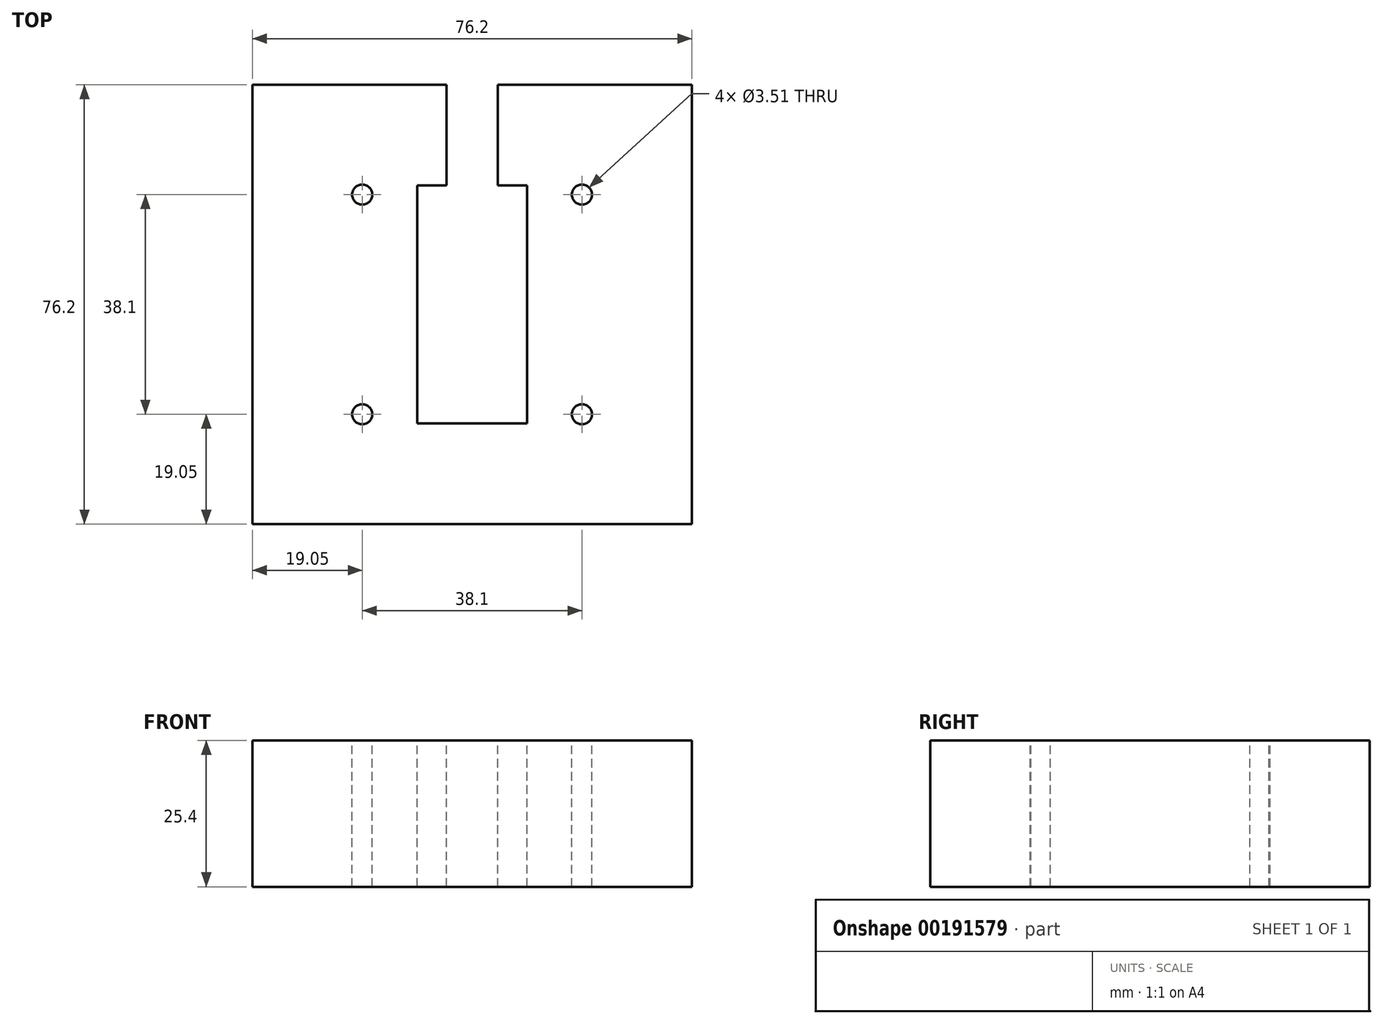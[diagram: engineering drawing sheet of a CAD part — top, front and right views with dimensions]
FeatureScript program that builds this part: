
annotation { "Feature Type Name" : "Feature", "Feature Type Description" : "" }
export const myFeature = defineFeature(function(context is Context, id is Id, definition is map)
    precondition{}
    {
        {
            var Q0;
            Q0=qCreatedBy(makeId("Top.planeOp"),FACE);
            var sketch = newSketch(context, id + "F0", { "sketchPlane" : qUnion([Q0])});
            skLineSegment(sketch, "E0.bottom", {"start": v(-38.1, 38.1) * mm, "end": v(38.1, 38.1) * mm});
            skLineSegment(sketch, "E0.top", {"start": v(-38.1, -38.1) * mm, "end": v(38.1, -38.1) * mm});
            skLineSegment(sketch, "E0.left", {"start": v(-38.1, 38.1) * mm, "end": v(-38.1, -38.1) * mm});
            skLineSegment(sketch, "E0.right", {"start": v(38.1, 38.1) * mm, "end": v(38.1, -38.1) * mm});
            skPoint(sketch, "E0.middle", {"position": v(0, 0) * mm});
            skSolve(sketch);
        }
        {
            var Q0;
            Q0 = qSketchRegion(id + "F0", true);
            extrude(context, id + "F1", {"entities" : qUnion([Q0]), "depth" : 25.4 * mm});
        }
        {
            var Q0;
            Q0=makeQuery(id+"F1.opExtrude","CAP_FACE",FACE,{"disambiguationData":[OSD([sQuery(id+"F0.wireOp",EDGE,"E0.bottom"),sQuery(id+"F0.wireOp",EDGE,"E0.top"),sQuery(id+"F0.wireOp",EDGE,"E0.left"),sQuery(id+"F0.wireOp",EDGE,"E0.right")])],"isStart":false});
            var sketch = newSketch(context, id + "F2", { "sketchPlane" : qUnion([Q0])});
            skLineSegment(sketch, "E1.bottom", {"start": v(-9.53, 20.64) * mm, "end": v(9.52, 20.64) * mm});
            skLineSegment(sketch, "E1.top", {"start": v(-9.53, -20.64) * mm, "end": v(9.52, -20.64) * mm});
            skLineSegment(sketch, "E1.left", {"start": v(-9.53, 20.64) * mm, "end": v(-9.53, -20.64) * mm});
            skLineSegment(sketch, "E1.right", {"start": v(9.53, 20.64) * mm, "end": v(9.52, -20.64) * mm});
            skPoint(sketch, "E1.middle", {"position": v(0, 0) * mm});
            skSolve(sketch);
        }
        {
            var Q0;
            Q0=makeQuery(id+"F2.imprint","IMPRINT",FACE,{"disambiguationData":[TD([[makeQuery(id+"F2.imprint","IMPRINT",EDGE,{"derivedFrom":sQuery(id+"F2.wireOp",EDGE,"E1.bottom")}),-1.0]])]});
            extrude(context, id + "F3", {"entities" : qUnion([Q0]), "operationType" : NewBodyOperationType.REMOVE, "oppositeDirection" : true, "depth" : 25.4 * mm});
        }
        {
            var Q0;
            Q0=makeQuery(id+"F1.opExtrude","CAP_FACE",FACE,{"disambiguationData":[OSD([sQuery(id+"F0.wireOp",EDGE,"E0.bottom"),sQuery(id+"F0.wireOp",EDGE,"E0.top"),sQuery(id+"F0.wireOp",EDGE,"E0.left"),sQuery(id+"F0.wireOp",EDGE,"E0.right")])],"isStart":false});
            var sketch = newSketch(context, id + "F4", { "sketchPlane" : qUnion([Q0])});
            skLineSegment(sketch, "E2.bottom", {"start": v(-4.45, 38.1) * mm, "end": v(4.45, 38.1) * mm});
            skLineSegment(sketch, "E2.top", {"start": v(-4.45, -38.1) * mm, "end": v(4.45, -38.1) * mm});
            skLineSegment(sketch, "E2.left", {"start": v(-4.45, 38.1) * mm, "end": v(-4.45, -38.1) * mm});
            skLineSegment(sketch, "E2.right", {"start": v(4.45, 38.1) * mm, "end": v(4.45, -38.1) * mm});
            skPoint(sketch, "E2.middle", {"position": v(0, 0) * mm});
            skLineSegment(sketch, "E3.bottom", {"start": v(4.45, 20.64) * mm, "end": v(-4.45, 20.64) * mm});
            skLineSegment(sketch, "E3.top", {"start": v(4.45, 38.1) * mm, "end": v(-4.45, 38.1) * mm});
            skLineSegment(sketch, "E3.left", {"start": v(4.45, 20.64) * mm, "end": v(4.45, 38.1) * mm});
            skLineSegment(sketch, "E3.right", {"start": v(-4.45, 20.64) * mm, "end": v(-4.45, 38.1) * mm});
            skSolve(sketch);
        }
        {
            var Q0;
            Q0=makeQuery(id+"F4.imprint","IMPRINT",FACE,{"disambiguationData":[TD([[makeQuery(id+"F4.imprint","IMPRINT",EDGE,{"derivedFrom":sQuery(id+"F4.wireOp",EDGE,"E3.bottom")}),1.0]])]});
            extrude(context, id + "F5", {"entities" : qUnion([Q0]), "operationType" : NewBodyOperationType.REMOVE, "oppositeDirection" : true, "depth" : 25.4 * mm});
        }
        {
            var Q0;
            Q0=makeQuery(id+"F1.opExtrude","CAP_FACE",FACE,{"disambiguationData":[OSD([sQuery(id+"F0.wireOp",EDGE,"E0.bottom"),sQuery(id+"F0.wireOp",EDGE,"E0.top"),sQuery(id+"F0.wireOp",EDGE,"E0.left"),sQuery(id+"F0.wireOp",EDGE,"E0.right")])],"isStart":false});
            var sketch = newSketch(context, id + "F6", { "sketchPlane" : qUnion([Q0])});
            skLineSegment(sketch, "E4.bottom", {"start": v(-38.1, -38.1) * mm, "end": v(-19.05, -38.1) * mm});
            skLineSegment(sketch, "E4.top", {"start": v(-38.1, -19.05) * mm, "end": v(-19.05, -19.05) * mm});
            skLineSegment(sketch, "E4.left", {"start": v(-38.1, -38.1) * mm, "end": v(-38.1, -19.05) * mm});
            skLineSegment(sketch, "E4.right", {"start": v(-19.05, -38.1) * mm, "end": v(-19.05, -19.05) * mm});
            skLineSegment(sketch, "E5.bottom", {"start": v(38.1, -38.1) * mm, "end": v(19.05, -38.1) * mm});
            skLineSegment(sketch, "E5.top", {"start": v(38.1, -19.05) * mm, "end": v(19.05, -19.05) * mm});
            skLineSegment(sketch, "E5.left", {"start": v(38.1, -38.1) * mm, "end": v(38.1, -19.05) * mm});
            skLineSegment(sketch, "E5.right", {"start": v(19.05, -38.1) * mm, "end": v(19.05, -19.05) * mm});
            skLineSegment(sketch, "E6.bottom", {"start": v(38.1, 38.1) * mm, "end": v(19.05, 38.1) * mm});
            skLineSegment(sketch, "E6.top", {"start": v(38.1, 19.05) * mm, "end": v(19.05, 19.05) * mm});
            skLineSegment(sketch, "E6.left", {"start": v(38.1, 38.1) * mm, "end": v(38.1, 19.05) * mm});
            skLineSegment(sketch, "E6.right", {"start": v(19.05, 38.1) * mm, "end": v(19.05, 19.05) * mm});
            skLineSegment(sketch, "E7.bottom", {"start": v(-38.1, 38.1) * mm, "end": v(-19.05, 38.1) * mm});
            skLineSegment(sketch, "E7.top", {"start": v(-38.1, 19.05) * mm, "end": v(-19.05, 19.05) * mm});
            skLineSegment(sketch, "E7.left", {"start": v(-38.1, 38.1) * mm, "end": v(-38.1, 19.05) * mm});
            skLineSegment(sketch, "E7.right", {"start": v(-19.05, 38.1) * mm, "end": v(-19.05, 19.05) * mm});
            skPoint(sketch, "E8", {"position": v(-19.05, 19.05) * mm});
            skPoint(sketch, "E9", {"position": v(19.05, 19.05) * mm});
            skPoint(sketch, "E10", {"position": v(19.05, -19.05) * mm});
            skPoint(sketch, "E11", {"position": v(-19.05, -19.05) * mm});
            skSolve(sketch);
        }
        {
            var Q0;
            Q0=sQuery(id+"F6.wireOp",VERTEX,"E8");
            var Q1;
            Q1=sQuery(id+"F6.wireOp",VERTEX,"E11");
            var Q2;
            Q2=sQuery(id+"F6.wireOp",VERTEX,"E10");
            var Q3;
            Q3=sQuery(id+"F6.wireOp",VERTEX,"E9");
            var Q4;
            Q4=makeQuery(id+"F1.opExtrude","SWEPT_BODY",BODY,{"disambiguationData":[OSD([sQuery(id+"F0.wireOp",EDGE,"E0.bottom"),sQuery(id+"F0.wireOp",EDGE,"E0.top"),sQuery(id+"F0.wireOp",EDGE,"E0.left"),sQuery(id+"F0.wireOp",EDGE,"E0.right")])]});
            hole(context, id + "F7", {"style" : HoleStyle.SIMPLE, "endStyle" : HoleEndStyle.THROUGH, "holeDiameter" : 3.5 * mm, "locations" : qUnion([Q0, Q1, Q2, Q3]), "scope" : qUnion([Q4]), "isTappedThrough" : true});
        }
    });
